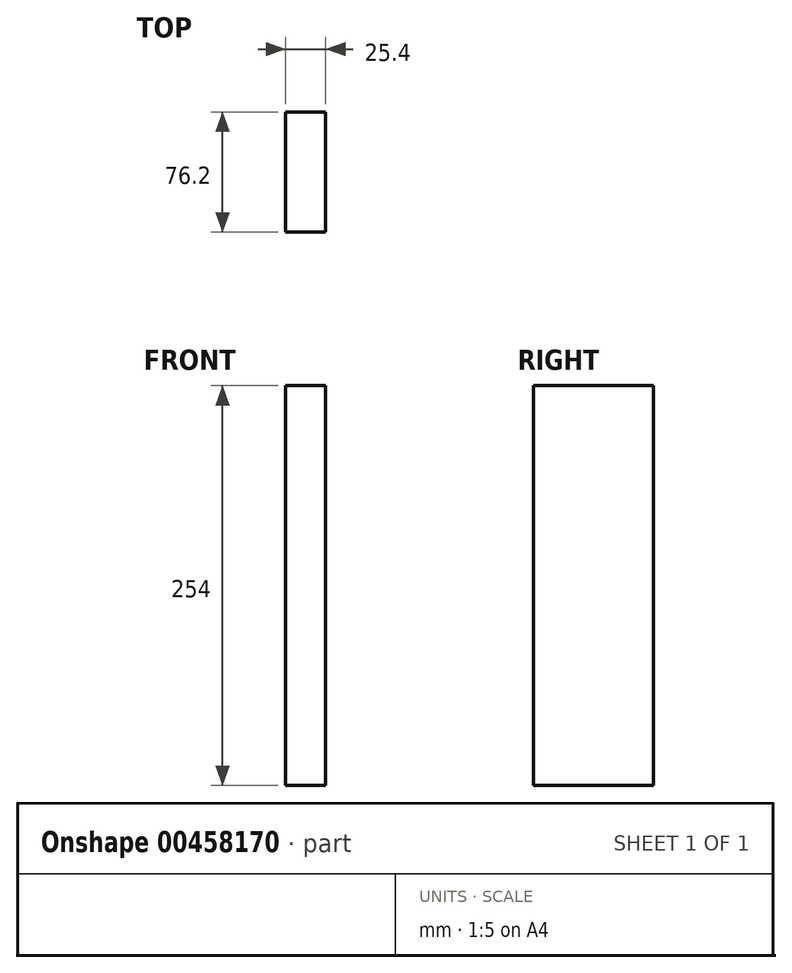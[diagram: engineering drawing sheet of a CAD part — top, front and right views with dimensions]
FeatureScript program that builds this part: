
annotation { "Feature Type Name" : "Feature", "Feature Type Description" : "" }
export const myFeature = defineFeature(function(context is Context, id is Id, definition is map)
    precondition{}
    {
        {
            var Q0;
            Q0=qCreatedBy(makeId("Top.planeOp"),FACE);
            var sketch = newSketch(context, id + "F0", { "sketchPlane" : qUnion([Q0])});
            skLineSegment(sketch, "E0.bottom", {"start": v(-4.7, 41.13) * mm, "end": v(20.7, 41.13) * mm});
            skLineSegment(sketch, "E0.top", {"start": v(-4.7, -35.07) * mm, "end": v(20.7, -35.07) * mm});
            skLineSegment(sketch, "E0.left", {"start": v(-4.7, 41.13) * mm, "end": v(-4.7, -35.07) * mm});
            skLineSegment(sketch, "E0.right", {"start": v(20.7, 41.13) * mm, "end": v(20.7, -35.07) * mm});
            skSolve(sketch);
        }
        {
            var Q0;
            Q0 = qSketchRegion(id + "F0", true);
            extrude(context, id + "F1", {"entities" : qUnion([Q0]), "depth" : 254 * mm});
        }
    });
